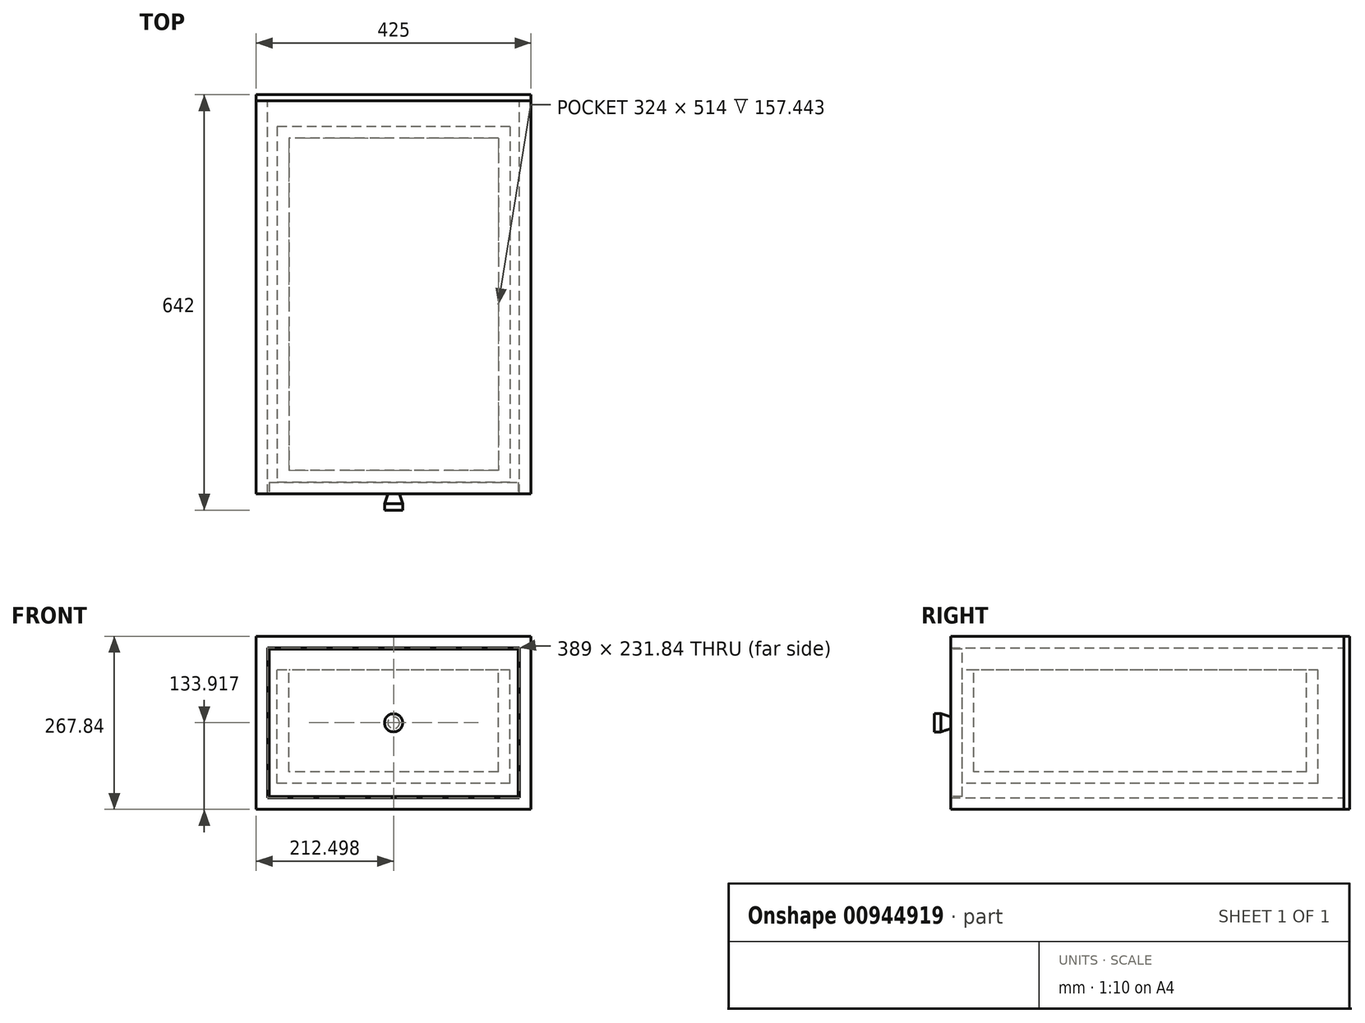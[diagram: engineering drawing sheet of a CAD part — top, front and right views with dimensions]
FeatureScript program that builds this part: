
annotation { "Feature Type Name" : "Feature", "Feature Type Description" : "" }
export const myFeature = defineFeature(function(context is Context, id is Id, definition is map)
    precondition{}
    {
        {
            var Q0;
            Q0=qCreatedBy(makeId("Front.planeOp"),FACE);
            var sketch = newSketch(context, id + "F0", { "sketchPlane" : qUnion([Q0])});
            skLineSegment(sketch, "E0", {"start": v(-301.33, -55.46) * mm, "end": v(-301.33, 212.38) * mm});
            skLineSegment(sketch, "E1", {"start": v(123.67, -55.46) * mm, "end": v(-301.33, -55.46) * mm});
            skLineSegment(sketch, "E2.1", {"start": v(-283.33, -37.46) * mm, "end": v(-283.33, 194.38) * mm});
            skLineSegment(sketch, "E3.trimOffspring", {"start": v(105.67, -37.46) * mm, "end": v(-283.33, -37.46) * mm});
            skLineSegment(sketch, "E4.top", {"start": v(-283.33, 194.38) * mm, "end": v(105.67, 194.38) * mm});
            skLineSegment(sketch, "E5.trimOffspring", {"start": v(105.67, 194.38) * mm, "end": v(105.67, -37.46) * mm});
            skLineSegment(sketch, "E6", {"start": v(-301.33, 212.38) * mm, "end": v(123.67, 212.38) * mm});
            skLineSegment(sketch, "E7", {"start": v(123.67, -55.46) * mm, "end": v(123.67, 212.38) * mm});
            skSolve(sketch);
        }
        {
            var Q0;
            Q0 = qSketchRegion(id + "F0", true);
            extrude(context, id + "F1", {"entities" : qUnion([Q0]), "depth" : 608 * mm, "offsetDistance" : 25 * mm});
        }
        {
            var Q0;
            Q0=makeQuery(id+"F1.opExtrude","CAP_FACE",FACE,{"disambiguationData":[OSD([sQuery(id+"F0.wireOp",EDGE,"E0"),sQuery(id+"F0.wireOp",EDGE,"E1"),sQuery(id+"F0.wireOp",EDGE,"E2.1"),sQuery(id+"F0.wireOp",EDGE,"E3.trimOffspring"),sQuery(id+"F0.wireOp",EDGE,"E4.top"),sQuery(id+"F0.wireOp",EDGE,"E5.trimOffspring"),sQuery(id+"F0.wireOp",EDGE,"E6"),sQuery(id+"F0.wireOp",EDGE,"E7")])],"isStart":true});
            var sketch = newSketch(context, id + "F2", { "sketchPlane" : qUnion([Q0])});
            skLineSegment(sketch, "E8.bottom", {"start": v(-123.67, -55.46) * mm, "end": v(301.33, -55.46) * mm});
            skLineSegment(sketch, "E8.top", {"start": v(-123.67, 212.38) * mm, "end": v(301.33, 212.38) * mm});
            skLineSegment(sketch, "E8.left", {"start": v(-123.67, -55.46) * mm, "end": v(-123.67, 212.38) * mm});
            skLineSegment(sketch, "E8.right", {"start": v(301.33, -55.46) * mm, "end": v(301.33, 212.38) * mm});
            skSolve(sketch);
        }
        {
            var Q0;
            Q0 = qSketchRegion(id + "F2", true);
            extrude(context, id + "F3", {"entities" : qUnion([Q0]), "depth" : 9 * mm, "offsetDistance" : 25 * mm});
        }
        {
            var Q0;
            Q0=makeQuery(id+"F1.opExtrude","CAP_FACE",FACE,{"disambiguationData":[OSD([sQuery(id+"F0.wireOp",EDGE,"E0"),sQuery(id+"F0.wireOp",EDGE,"E1"),sQuery(id+"F0.wireOp",EDGE,"E2.1"),sQuery(id+"F0.wireOp",EDGE,"E3.trimOffspring"),sQuery(id+"F0.wireOp",EDGE,"E4.top"),sQuery(id+"F0.wireOp",EDGE,"E5.trimOffspring"),sQuery(id+"F0.wireOp",EDGE,"E6"),sQuery(id+"F0.wireOp",EDGE,"E7")])],"isStart":false});
            var sketch = newSketch(context, id + "F4", { "sketchPlane" : qUnion([Q0])});
            skLineSegment(sketch, "E9.0", {"start": v(-281.33, 192.38) * mm, "end": v(103.67, 192.38) * mm});
            skLineSegment(sketch, "E9.1", {"start": v(-281.33, -35.46) * mm, "end": v(-281.33, 192.38) * mm});
            skLineSegment(sketch, "E9.2", {"start": v(103.67, -35.46) * mm, "end": v(-281.33, -35.46) * mm});
            skLineSegment(sketch, "E9.3", {"start": v(103.67, 192.38) * mm, "end": v(103.67, -35.46) * mm});
            skSolve(sketch);
        }
        {
            var Q0;
            Q0 = qSketchRegion(id + "F4", true);
            extrude(context, id + "F5", {"entities" : qUnion([Q0]), "oppositeDirection" : true, "depth" : 18 * mm, "offsetDistance" : 25 * mm});
        }
        {
            var Q0;
            Q0=makeQuery(id+"F5.opExtrude","CAP_FACE",FACE,{"disambiguationData":[OSD([sQuery(id+"F4.wireOp",EDGE,"E9.0"),sQuery(id+"F4.wireOp",EDGE,"E9.1"),sQuery(id+"F4.wireOp",EDGE,"E9.2"),sQuery(id+"F4.wireOp",EDGE,"E9.3")])],"isStart":false});
            var sketch = newSketch(context, id + "F6", { "sketchPlane" : qUnion([Q0])});
            skLineSegment(sketch, "E10.bottom", {"start": v(-91.17, -15.46) * mm, "end": v(268.83, -15.46) * mm});
            skLineSegment(sketch, "E10.top", {"start": v(-91.17, 159.98) * mm, "end": v(268.83, 159.98) * mm});
            skLineSegment(sketch, "E10.left", {"start": v(-91.17, -15.46) * mm, "end": v(-91.17, 159.98) * mm});
            skLineSegment(sketch, "E10.right", {"start": v(268.83, -15.46) * mm, "end": v(268.83, 159.98) * mm});
            skSolve(sketch);
        }
        {
            var Q0;
            Q0 = qSketchRegion(id + "F6", true);
            extrude(context, id + "F7", {"entities" : qUnion([Q0]), "depth" : 550 * mm, "offsetDistance" : 25 * mm});
        }
        {
            var Q0;
            Q0=makeQuery(id+"F7.opExtrude","SWEPT_FACE",FACE,{"disambiguationData":[OSD([sQuery(id+"F6.wireOp",EDGE,"E10.top")])]});
            shell(context, id + "F8", {"entities" : qUnion([Q0]), "thickness" : 18 * mm});
        }
        {
            var Q0;
            Q0=makeQuery(id+"F5.opExtrude","CAP_FACE",FACE,{"disambiguationData":[OSD([sQuery(id+"F4.wireOp",EDGE,"E9.0"),sQuery(id+"F4.wireOp",EDGE,"E9.1"),sQuery(id+"F4.wireOp",EDGE,"E9.2"),sQuery(id+"F4.wireOp",EDGE,"E9.3")])],"isStart":true});
            var sketch = newSketch(context, id + "F9", { "sketchPlane" : qUnion([Q0])});
            skCircle(sketch, "E11", {"center": v(-88.83, 78.46) * mm, "radius": 14.01 * mm});
            skSolve(sketch);
        }
        {
            var Q0;
            Q0 = qSketchRegion(id + "F9", true);
            extrude(context, id + "F10", {"entities" : qUnion([Q0]), "depth" : 25 * mm, "offsetDistance" : 25 * mm});
        }
        {
            var Q0;
            Q0=makeQuery(id+"F10.opExtrude","CAP_EDGE",EDGE,{"disambiguationData":[OSD([sQuery(id+"F9.wireOp",EDGE,"E11")])],"isStart":true});
            chamfer(context, id + "F11", {"entities" : qUnion([Q0]), "chamferType" : ChamferType.TWO_OFFSETS, "width1" : 15 * mm, "oppositeDirection" : false, "width2" : 5 * mm, "tangentPropagation" : true});
        }
    });
